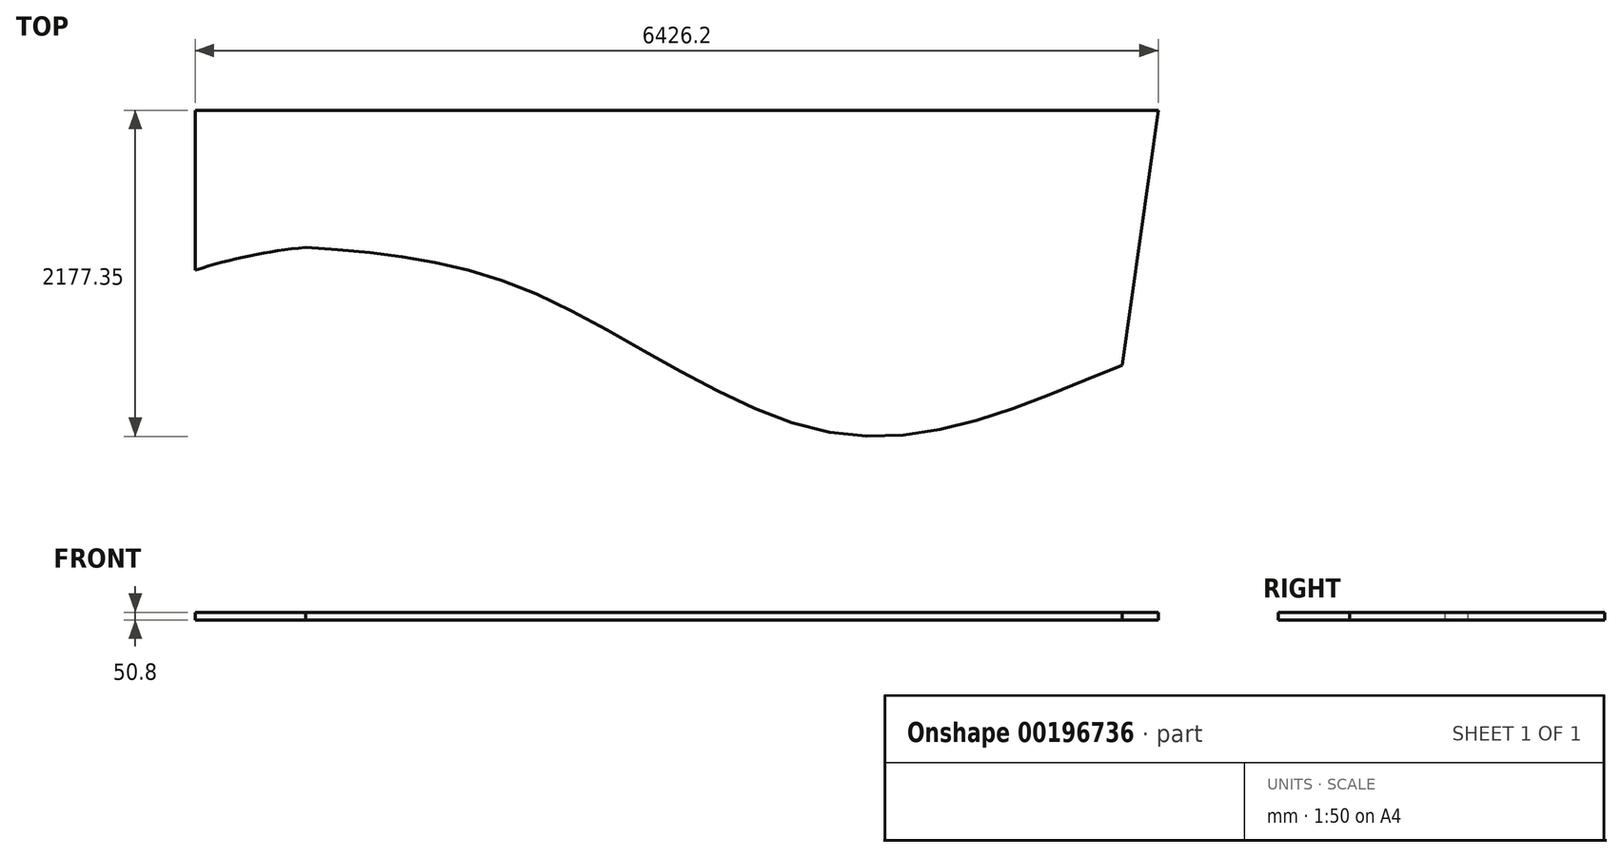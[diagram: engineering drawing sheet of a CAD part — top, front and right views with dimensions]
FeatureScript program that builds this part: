
annotation { "Feature Type Name" : "Feature", "Feature Type Description" : "" }
export const myFeature = defineFeature(function(context is Context, id is Id, definition is map)
    precondition{}
    {
        {
            var Q0;
            Q0=qCreatedBy(makeId("Top.planeOp"),FACE);
            var sketch = newSketch(context, id + "F0", { "sketchPlane" : qUnion([Q0])});
            skLineSegment(sketch, "E0", {"start": v(0, 0) * mm, "end": v(0, 5181.6) * mm});
            skLineSegment(sketch, "E1", {"start": v(0, 0) * mm, "end": v(5689.6, 0) * mm});
            skLineSegment(sketch, "E2", {"start": v(0, 5181.6) * mm, "end": v(6426.2, 5181.6) * mm});
            skLineSegment(sketch, "E3", {"start": v(6426.2, 5181.6) * mm, "end": v(5689.6, 0) * mm});
            skPoint(sketch, "E4", {"position": v(6184.28, 3479.8) * mm});
            skPoint(sketch, "E5", {"position": v(5929.11, 1684.86) * mm});
            skPoint(sketch, "E6", {"position": v(0, 3022.6) * mm});
            skLineSegment(sketch, "E7", {"start": v(0, 3022.6) * mm, "end": v(6119.28, 3022.6) * mm, "construction": true});
            skPoint(sketch, "E8", {"position": v(0, 4114.8) * mm});
            skPoint(sketch, "E9", {"position": v(736.6, 3022.6) * mm});
            skLineSegment(sketch, "E10", {"start": v(736.6, 3022.6) * mm, "end": v(736.6, 5181.6) * mm, "construction": true});
            skLineSegment(sketch, "E11", {"start": v(0, 4114.8) * mm, "end": v(6274.55, 4114.8) * mm, "construction": true});
            skPoint(sketch, "E12", {"position": v(736.6, 4267.2) * mm});
            skLineSegment(sketch, "E13", {"start": v(0, 4267.2) * mm, "end": v(6296.21, 4267.2) * mm, "construction": true});
            skPoint(sketch, "E14", {"position": v(4292.6, 5181.6) * mm});
            skLineSegment(sketch, "E15", {"start": v(4292.6, 5181.6) * mm, "end": v(4292.6, 3022.6) * mm, "construction": true});
            skPoint(sketch, "E16", {"position": v(1473.2, 3022.6) * mm});
            skLineSegment(sketch, "E17", {"start": v(1473.2, 3022.6) * mm, "end": v(1473.2, 5181.6) * mm, "construction": true});
            skLineSegment(sketch, "E18", {"start": v(6426.2, 5181.6) * mm, "end": v(6184.28, 3479.8) * mm});
            skArc(sketch, "E19", {"start": v(736.6, 4267.2) * mm, "mid": v(364.26, 4210.52) * mm, "end": v(0, 4114.8) * mm});
            skLineSegment(sketch, "E20", {"start": v(2260.6, 5181.6) * mm, "end": v(2260.6, 3022.6) * mm, "construction": true});
            skPoint(sketch, "E21", {"position": v(2260.6, 3962.4) * mm});
            skFitSpline(sketch, "E22", {"points": [v(6184.28, 3479.8) * mm, v(4292.6, 3022.6) * mm, v(2260.6, 3962.4) * mm, v(736.6, 4267.2) * mm], "startDerivative": vector(-5566.32, -2255.46) * mm, "endDerivative": vector(-4923.14, 347.12) * mm});
            skPoint(sketch, "E23", {"position": v(3278.9, 3416.45) * mm});
            skSolve(sketch);
        }
        {
            var Q0;
            {var subQ0=sQuery(id+"F0.wireOp",EDGE,"E2");Q0=makeQuery(id+"F0.imprint","IMPRINT",FACE,{"disambiguationData":[TD([[makeQuery(id+"F0.imprint","IMPRINT",EDGE,{"derivedFrom":subQ0}),-1.0]])]});}
            extrude(context, id + "F1", {"entities" : qUnion([Q0]), "depth" : 50.8 * mm});
        }
    });
